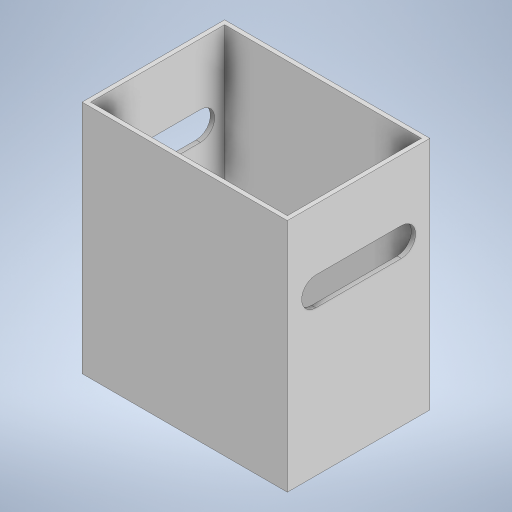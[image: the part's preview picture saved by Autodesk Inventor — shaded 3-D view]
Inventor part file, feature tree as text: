
AUTODESK INVENTOR PART (.ipt)
format: ipt  version: 2024 (Build 280153000, 153)  size: 220,160 bytes
history: native  units: mm
features: extrude x3, sketch x3
ambient origin geometry x8: Origin, YZ Plane, XZ Plane, XY Plane, X Axis, Y Axis, Z Axis, Center Point
bodies: Body1 (feature_tree)
feature tree (6):
  extrude  "Extrusión2"  Depth=50.0mm
  extrude  "Extrusión3"  Depth=1.5mm
  extrude  "Extrusión4"  Depth=1.5mm
  sketch  "Boceto3"  dims[d8=72.0mm d9=50.0mm]
  sketch  "Boceto5"  dims[d10=82.5mm d11=0.0mm d12=1.5mm]
  sketch  "Boceto6"  dims[d13=1.5mm d14=1.5mm d15=1.5mm d16=81.0mm d17=0.0mm d18=21.5mm d19=40.0mm d20=10.0mm d21=5.0mm d22=0.0mm d23=0.0mm]
